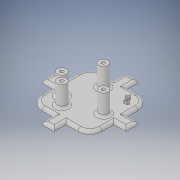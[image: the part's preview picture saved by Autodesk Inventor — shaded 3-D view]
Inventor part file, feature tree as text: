
AUTODESK INVENTOR PART (.ipt)
format: ipt  version: 2018 (Build 220112000, 112)  size: 387,072 bytes
history: native  units: in
note: dims shown in document units (in); Inventor stores cm internally (conversion verified against a paired STEP export)
features: other x4, fillet x3, sketch x3, extrude x2, move_body x1, emboss x1
ambient origin geometry x8: Origin, YZ Plane, XZ Plane, XY Plane, X Axis, Y Axis, Z Axis, Center Point
bodies: Solid5 (feature_tree)
feature tree (14):
  other  "Remote Top.ipt"
  move_body  "Move Body1"
  extrude  "Extrusion1"  Depth=0.3937in TaperAngle=0.0deg
  extrude  "Extrusion2"  Depth=0.125in
  fillet  "Fillet3"  Radius=0.125in
  fillet  "Fillet4"  Radius=0.125in
  fillet  "Fillet5"  Radius=0.01in
  emboss  "Emboss1"
  other  "Magnet Sketch"
  other  "Solid31::Remote Top.ipt"
  other  "TaggingFeature2"
  sketch  "Sketch2"  dims[d0=0.3937in d1=0.0in d2=1.0in d3=0.0in]
  sketch  "Sketch3"  dims[d4=0.125in d5=0.125in d6=0.125in d7=0.125in d8=0.01in]
  sketch  "Sketch4"  dims[d9=0.01in d10=0.01in d11=0.01in d12=1.0in d13=0.0in d14=1.25in d15=1.25in d16=1.25in d17=1.25in d18=0.5in d19=0.5in d20=0.5in d21=0.25in d22=1.5748in d24=360.0deg d26=0.125in d27=0.0in d30=0.125in d31=0.1in d32=0.1in d33=0.05in d34=0.0in]
